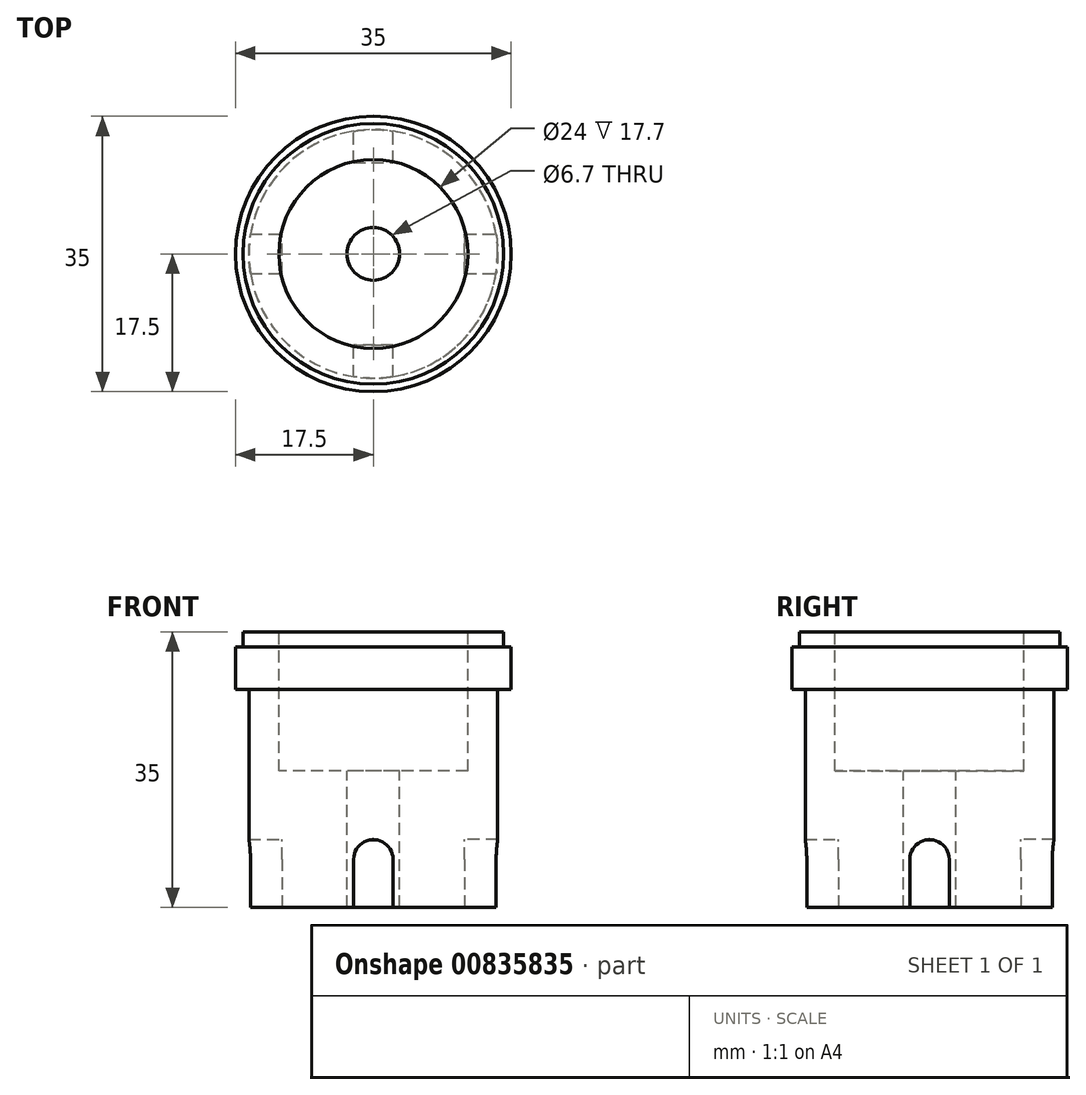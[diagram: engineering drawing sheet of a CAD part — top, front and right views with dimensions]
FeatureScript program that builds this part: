
annotation { "Feature Type Name" : "Feature", "Feature Type Description" : "" }
export const myFeature = defineFeature(function(context is Context, id is Id, definition is map)
    precondition{}
    {
        {
            var Q0;
            Q0=qCreatedBy(makeId("Top.planeOp"),FACE);
            var sketch = newSketch(context, id + "F0", { "sketchPlane" : qUnion([Q0])});
            skCircle(sketch, "E0", {"center": v(0, 0) * mm, "radius": 15.8 * mm});
            skSolve(sketch);
        }
        {
            var Q0;
            Q0=makeQuery(id+"F0.imprint","IMPRINT",FACE,{"disambiguationData":[TD([[makeQuery(id+"F0.imprint","IMPRINT",EDGE,{"derivedFrom":sQuery(id+"F0.wireOp",EDGE,"E0")}),1.0]])]});
            extrude(context, id + "F1", {"entities" : qUnion([Q0]), "depth" : 27.7 * mm, "offsetDistance" : 25 * mm});
        }
        {
            var Q0;
            Q0=makeQuery(id+"F1.opExtrude","CAP_FACE",FACE,{"disambiguationData":[OSD([sQuery(id+"F0.wireOp",EDGE,"E0")])],"isStart":false});
            var sketch = newSketch(context, id + "F2", { "sketchPlane" : qUnion([Q0])});
            skCircle(sketch, "E1", {"center": v(0, 0) * mm, "radius": 17.5 * mm});
            skSolve(sketch);
        }
        {
            var Q0;
            Q0=makeQuery(id+"F2.imprint","IMPRINT",FACE,{"disambiguationData":[TD([[makeQuery(id+"F2.imprint","IMPRINT",EDGE,{"derivedFrom":sQuery(id+"F2.wireOp",EDGE,"E1")}),1.0]])]});
            var Q1;
            Q1=makeQuery(id+"F2.imprint","IMPRINT",FACE,{"disambiguationData":[TD([[makeQuery(id+"F2.imprint","IMPRINT",EDGE,{"derivedFrom":makeQuery(id+"F1.opExtrude","CAP_EDGE",EDGE,{"disambiguationData":[OSD([sQuery(id+"F0.wireOp",EDGE,"E0")])],"isStart":false})}),1.0]])]});
            extrude(context, id + "F3", {"entities" : qUnion([Q0, Q1]), "operationType" : NewBodyOperationType.ADD, "depth" : 5.4 * mm, "offsetDistance" : 25 * mm});
        }
        {
            var Q0;
            Q0=makeQuery(id+"F3.opExtrude","CAP_FACE",FACE,{"disambiguationData":[OSD([sQuery(id+"F2.wireOp",EDGE,"E1")])],"isStart":false});
            var sketch = newSketch(context, id + "F4", { "sketchPlane" : qUnion([Q0])});
            skCircle(sketch, "E2", {"center": v(0, 0) * mm, "radius": 16.55 * mm});
            skSolve(sketch);
        }
        {
            var Q0;
            Q0=makeQuery(id+"F4.imprint","IMPRINT",FACE,{"disambiguationData":[TD([[makeQuery(id+"F4.imprint","IMPRINT",EDGE,{"derivedFrom":sQuery(id+"F4.wireOp",EDGE,"E2")}),1.0]])]});
            extrude(context, id + "F5", {"entities" : qUnion([Q0]), "operationType" : NewBodyOperationType.ADD, "depth" : 1.9 * mm, "offsetDistance" : 25 * mm});
        }
        {
            var Q0;
            Q0=makeQuery(id+"F1.opExtrude","CAP_FACE",FACE,{"disambiguationData":[OSD([sQuery(id+"F0.wireOp",EDGE,"E0")])],"isStart":true});
            var sketch = newSketch(context, id + "F6", { "sketchPlane" : qUnion([Q0])});
            skLineSegment(sketch, "E3.bottom", {"start": v(-11.6, 11.6) * mm, "end": v(11.6, 11.6) * mm});
            skLineSegment(sketch, "E3.top", {"start": v(-11.6, -11.6) * mm, "end": v(11.6, -11.6) * mm});
            skLineSegment(sketch, "E3.left", {"start": v(-11.6, 11.6) * mm, "end": v(-11.6, -11.6) * mm});
            skLineSegment(sketch, "E3.right", {"start": v(11.6, 11.6) * mm, "end": v(11.6, -11.6) * mm});
            skLineSegment(sketch, "E4", {"start": v(2.5, 15.6) * mm, "end": v(2.5, -15.6) * mm});
            skLineSegment(sketch, "E5", {"start": v(-2.5, 15.6) * mm, "end": v(-2.5, -15.6) * mm});
            skLineSegment(sketch, "E6", {"start": v(-15.6, -2.5) * mm, "end": v(15.6, -2.5) * mm});
            skLineSegment(sketch, "E7", {"start": v(-15.6, 2.5) * mm, "end": v(15.6, 2.5) * mm});
            skSolve(sketch);
        }
        {
            var Q0;
            {var subQ0=sQuery(id+"F6.wireOp",EDGE,"E7");var subQ1=sQuery(id+"F6.wireOp",EDGE,"E3.right");var subQ2=makeQuery(id+"F6.imprint","INTERSECT",VERTEX,{"derivedFrom":[subQ1,subQ0]});Q0=makeQuery(id+"F6.imprint","IMPRINT",FACE,{"disambiguationData":[TD([[makeQuery(id+"F6.imprint","IMPRINT",EDGE,{"disambiguationData":[TD([[subQ2,-1.0]])],"derivedFrom":subQ1}),1.0]])]});}
            extrude(context, id + "F7", {"entities" : qUnion([Q0]), "operationType" : NewBodyOperationType.ADD, "oppositeDirection" : true, "depth" : 6.1 * mm, "offsetDistance" : 25 * mm});
        }
        {
            var Q0;
            {var subQ0=sQuery(id+"F6.wireOp",EDGE,"E5");var subQ1=sQuery(id+"F6.wireOp",EDGE,"E3.bottom");var subQ2=makeQuery(id+"F6.imprint","INTERSECT",VERTEX,{"derivedFrom":[subQ1,subQ0]});Q0=makeQuery(id+"F6.imprint","IMPRINT",FACE,{"disambiguationData":[TD([[makeQuery(id+"F6.imprint","IMPRINT",EDGE,{"disambiguationData":[TD([[subQ2,-1.0]])],"derivedFrom":subQ1}),1.0]])]});}
            extrude(context, id + "F8", {"entities" : qUnion([Q0]), "operationType" : NewBodyOperationType.REMOVE, "oppositeDirection" : true, "depth" : 6.1 * mm, "offsetDistance" : 25 * mm});
        }
        {
            var Q0;
            Q0=makeQuery(id+"F8.boolean.opBoolean","COPY",FACE,{"derivedFrom":makeQuery(id+"F8.opExtrude","SWEPT_FACE",FACE,{"disambiguationData":[OSD([sQuery(id+"F6.wireOp",EDGE,"E3.bottom")])]})});
            var sketch = newSketch(context, id + "F9", { "sketchPlane" : qUnion([Q0])});
            skCircle(sketch, "E8", {"center": v(0, 6.1) * mm, "radius": 2.5 * mm});
            skSolve(sketch);
        }
        {
            var Q0;
            {var subQ1=sQuery(id+"F6.wireOp",EDGE,"E3.bottom");Q0=makeQuery(id+"F9.imprint","IMPRINT",FACE,{"disambiguationData":[TD([[makeQuery(id+"F9.imprint","IMPRINT",EDGE,{"derivedFrom":makeQuery(id+"F8.boolean.opBoolean","COPY",EDGE,{"derivedFrom":makeQuery(id+"F8.opExtrude","CAP_EDGE",EDGE,{"disambiguationData":[OSD([subQ1])],"isStart":true})})}),1.0]])]});}
            var Q1;
            Q1 = qSketchRegion(id + "F9", true);
            extrude(context, id + "F10", {"entities" : qUnion([Q0, Q1]), "operationType" : NewBodyOperationType.REMOVE, "depth" : 25 * mm, "offsetDistance" : 25 * mm});
        }
        {
            var Q0;
            {var subQ0=sQuery(id+"F6.wireOp",EDGE,"E7");var subQ1=sQuery(id+"F6.wireOp",EDGE,"E3.left");var subQ2=makeQuery(id+"F6.imprint","INTERSECT",VERTEX,{"derivedFrom":[subQ1,subQ0]});Q0=makeQuery(id+"F6.imprint","IMPRINT",FACE,{"disambiguationData":[TD([[makeQuery(id+"F6.imprint","IMPRINT",EDGE,{"disambiguationData":[TD([[subQ2,-1.0]])],"derivedFrom":subQ1}),-1.0]])]});}
            var Q1;
            {var subQ0=sQuery(id+"F6.wireOp",EDGE,"E5");var subQ1=sQuery(id+"F6.wireOp",EDGE,"E3.top");var subQ2=makeQuery(id+"F6.imprint","INTERSECT",VERTEX,{"derivedFrom":[subQ1,subQ0]});Q1=makeQuery(id+"F6.imprint","IMPRINT",FACE,{"disambiguationData":[TD([[makeQuery(id+"F6.imprint","IMPRINT",EDGE,{"disambiguationData":[TD([[subQ2,-1.0]])],"derivedFrom":subQ1}),-1.0]])]});}
            var Q2;
            {var subQ0=sQuery(id+"F6.wireOp",EDGE,"E7");var subQ1=sQuery(id+"F6.wireOp",EDGE,"E3.right");var subQ2=makeQuery(id+"F6.imprint","INTERSECT",VERTEX,{"derivedFrom":[subQ1,subQ0]});Q2=makeQuery(id+"F6.imprint","IMPRINT",FACE,{"disambiguationData":[TD([[makeQuery(id+"F6.imprint","IMPRINT",EDGE,{"disambiguationData":[TD([[subQ2,-1.0]])],"derivedFrom":subQ1}),1.0]])]});}
            extrude(context, id + "F11", {"entities" : qUnion([Q0, Q1, Q2]), "operationType" : NewBodyOperationType.REMOVE, "oppositeDirection" : true, "depth" : 6.1 * mm, "offsetDistance" : 25 * mm});
        }
        {
            var Q0;
            Q0=makeQuery(id+"F11.boolean.opBoolean","COPY",FACE,{"derivedFrom":makeQuery(id+"F11.opExtrude","SWEPT_FACE",FACE,{"disambiguationData":[OSD([sQuery(id+"F6.wireOp",EDGE,"E3.left")])]})});
            var sketch = newSketch(context, id + "F12", { "sketchPlane" : qUnion([Q0])});
            skCircle(sketch, "E9", {"center": v(0, 6.1) * mm, "radius": 2.5 * mm});
            skSolve(sketch);
        }
        {
            var Q0;
            Q0 = qSketchRegion(id + "F12", true);
            extrude(context, id + "F13", {"entities" : qUnion([Q0]), "operationType" : NewBodyOperationType.REMOVE, "depth" : 25 * mm, "offsetDistance" : 25 * mm});
        }
        {
            var Q0;
            Q0=makeQuery(id+"F11.boolean.opBoolean","COPY",FACE,{"derivedFrom":makeQuery(id+"F11.opExtrude","SWEPT_FACE",FACE,{"disambiguationData":[OSD([sQuery(id+"F6.wireOp",EDGE,"E3.top")])]})});
            var sketch = newSketch(context, id + "F14", { "sketchPlane" : qUnion([Q0])});
            skCircle(sketch, "E10", {"center": v(0, 6.1) * mm, "radius": 2.5 * mm});
            skSolve(sketch);
        }
        {
            var Q0;
            {var subQ1=sQuery(id+"F6.wireOp",EDGE,"E3.top");var subQ2=makeQuery(id+"F11.boolean.opBoolean","COPY",EDGE,{"derivedFrom":makeQuery(id+"F11.opExtrude","CAP_EDGE",EDGE,{"disambiguationData":[OSD([subQ1])],"isStart":false})});Q0=makeQuery(id+"F14.imprint","IMPRINT",FACE,{"disambiguationData":[TD([[makeQuery(id+"F14.imprint","IMPRINT",EDGE,{"derivedFrom":subQ2}),-1.0]])]});}
            extrude(context, id + "F15", {"entities" : qUnion([Q0]), "operationType" : NewBodyOperationType.REMOVE, "depth" : 25 * mm, "offsetDistance" : 25 * mm});
        }
        {
            var Q0;
            Q0=makeQuery(id+"F11.boolean.opBoolean","COPY",FACE,{"derivedFrom":makeQuery(id+"F11.opExtrude","SWEPT_FACE",FACE,{"disambiguationData":[OSD([sQuery(id+"F6.wireOp",EDGE,"E3.right")])]})});
            var sketch = newSketch(context, id + "F16", { "sketchPlane" : qUnion([Q0])});
            skCircle(sketch, "E11", {"center": v(0, 6.1) * mm, "radius": 2.5 * mm});
            skSolve(sketch);
        }
        {
            var Q0;
            Q0 = qSketchRegion(id + "F16", true);
            extrude(context, id + "F17", {"entities" : qUnion([Q0]), "operationType" : NewBodyOperationType.REMOVE, "depth" : 25 * mm, "offsetDistance" : 25 * mm});
        }
        {
            var Q0;
            Q0=makeQuery(id+"F5.opExtrude","CAP_FACE",FACE,{"disambiguationData":[OSD([sQuery(id+"F4.wireOp",EDGE,"E2")])],"isStart":false});
            var sketch = newSketch(context, id + "F18", { "sketchPlane" : qUnion([Q0])});
            skCircle(sketch, "E12", {"center": v(0, 0) * mm, "radius": 12 * mm});
            skSolve(sketch);
        }
        {
            var Q0;
            Q0 = qSketchRegion(id + "F18", true);
            var Q1;
            Q1=makeQuery(id+"F18.imprint","IMPRINT",FACE,{"disambiguationData":[TD([[makeQuery(id+"F18.imprint","IMPRINT",EDGE,{"derivedFrom":sQuery(id+"F18.wireOp",EDGE,"E12")}),1.0]])]});
            extrude(context, id + "F19", {"entities" : qUnion([Q0, Q1]), "operationType" : NewBodyOperationType.REMOVE, "oppositeDirection" : true, "depth" : 17.7 * mm, "offsetDistance" : 25 * mm});
        }
        {
            var Q0;
            Q0=makeQuery(id+"F19.boolean.opBoolean","COPY",FACE,{"derivedFrom":makeQuery(id+"F19.opExtrude","CAP_FACE",FACE,{"disambiguationData":[OSD([sQuery(id+"F18.wireOp",EDGE,"E12")])],"isStart":false})});
            var sketch = newSketch(context, id + "F20", { "sketchPlane" : qUnion([Q0])});
            skCircle(sketch, "E13", {"center": v(0, 0) * mm, "radius": 3.35 * mm});
            skSolve(sketch);
        }
        {
            var Q0;
            Q0=makeQuery(id+"F20.imprint","IMPRINT",FACE,{"disambiguationData":[TD([[makeQuery(id+"F20.imprint","IMPRINT",EDGE,{"derivedFrom":sQuery(id+"F20.wireOp",EDGE,"E13")}),1.0]])]});
            extrude(context, id + "F21", {"entities" : qUnion([Q0]), "operationType" : NewBodyOperationType.REMOVE, "oppositeDirection" : true, "depth" : 33.4 * mm, "offsetDistance" : 25 * mm});
        }
    });
